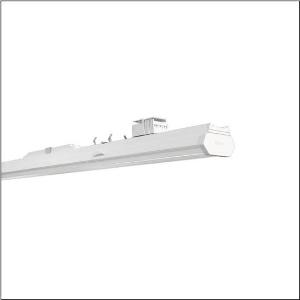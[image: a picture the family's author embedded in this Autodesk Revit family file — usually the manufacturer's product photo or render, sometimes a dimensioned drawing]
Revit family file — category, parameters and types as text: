
# Revit family: licross_21_protected_mo_52tp117n485g
name_source: partatom
category: Lighting Fixtures
units: mm (PartAtom-declared; Revit-internal decimal feet)

## family parameters
Cut with Voids When Loaded = No
Host = Face
Light Source = No
Part Type = Normal
Room Calculation Point = No
Round Connector Dimension = Use Diameter
Shared = No

## types (1)
- Licross 21 Protected MO (1 x LED, 8570 lm, 47.9 W, 4000K)
    Apparent Load = 48 VA
    CIE Flux Codes = 83 94 98 100 100
    Color Rendering = 80
    Color Temperature = 4000K
    Default Elevation = 1800 mm
    Description = Licross 21 Protected MO, luminaire insert, of sheet steel, galvanised, coil coated, white, length: 1.500mm, width: 66mm, height: 67mm, LED rated luminous flux: 8.570lm, light colour: 840, SDCM (Standard Deviation of Colour Matching)MacAdam ≤ 3 SDCM (initial), control gear: ON/OFF, with plug, 3-pole, with phase selection, mains connection: 220..240V, AC, 50/60Hz, rated input power: 48W, internal wiring halogen-free, primary light control with lens, of plastic, primary optical cover: cover, of PMMA, light emission: direct distribution, primary light characteristic: symmetric, protection rating (complete): IP64, insulation class (complete): insulation class I (protective earthing), certification: CE, ENEC, VDE, UKCA, protection symbol: D if used in an environment with conductive dust loads with corresponding accessories, impact resistance: IK06, permissible ambient temperature for indoor applications: -35..+45°C, corresponds to IFS (International Featured Standards) requirements for safety and quality in the food industry, reducing of maximum allowable ambient temperature of 5°C with ceiling mounting, LABS conformity tested according to VDMA 24364:2018-05, The light source and the operating device comply with the requirements of the Ecodesign Regulation (EU) 2019/2020 and are replaceable in accordance with this regulation, packaging unit: 1 piece
    Height = 92 mm
    Lamp = 1 x LED
    Lamp Light Flux = 8570 lm
    Lamp Power = 47.9 W
    Lamp count = 1
    Length = 1500 mm
    Luminous efficacy = 179 lm/W
    Manufacturer = Siteco
    ModVariant = No
    Model = 52TP117N485G
    Mounting Place = Ceiling
    Mounting Type = Pendant
    Number of Poles = 1
    OnlyDefault = Yes
    Power Factor = 1
    Product Name = Licross 21 Protected MO
    Product group = luminaire insert | ceiling pendant
    ProductGroupID = 901
    Protection Class = Protection class I
    Protection Degree = IP 64
    RLX_Detail_Level = 1
    RLX_Emergency_Light_Flux = 0 lm
    RLX_Emergency_Type = 0
    RLX_Emergency_Type_DB = No
    RlxData = <blob elided: 20653 chars, md5=240564b2>
    Socket = socket
    Standby Power = 0 W
    System Light Flux = 8570 lm
    System Power = 48 W
    Type Comments = Product without accessories
    Type Image = l_1256148.jpg
    URL = http://relux.com
    VarID = ---
    Voltage = 0 V
    Weight = 0.00 kg
    Width = 88 mm

## geometry (parser evidence)
native form markers: Blend x4, Sweep x12
no freeform markers — native parametric forms only
